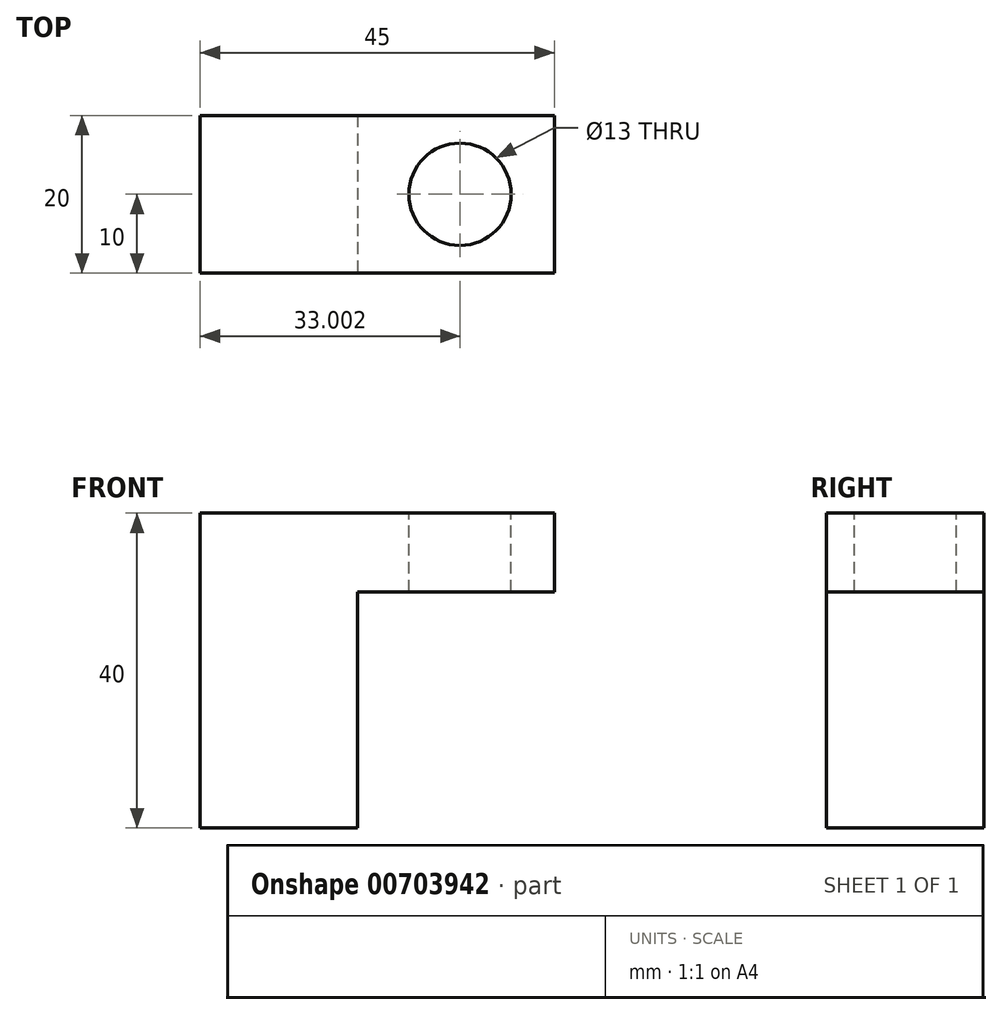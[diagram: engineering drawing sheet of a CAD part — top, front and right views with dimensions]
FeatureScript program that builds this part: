
annotation { "Feature Type Name" : "Feature", "Feature Type Description" : "" }
export const myFeature = defineFeature(function(context is Context, id is Id, definition is map)
    precondition{}
    {
        {
            var Q0;
            Q0=qCreatedBy(makeId("Top.planeOp"),FACE);
            var sketch = newSketch(context, id + "F0", { "sketchPlane" : qUnion([Q0])});
            skLineSegment(sketch, "E0", {"start": v(-97.99, 0) * mm, "end": v(96.27, 0) * mm, "construction": true});
            skLineSegment(sketch, "E1.bottom", {"start": v(-87.99, 10) * mm, "end": v(-107.99, 10) * mm});
            skLineSegment(sketch, "E1.top", {"start": v(-87.99, -10) * mm, "end": v(-107.99, -10) * mm});
            skLineSegment(sketch, "E1.left", {"start": v(-87.99, 10) * mm, "end": v(-87.99, -10) * mm});
            skLineSegment(sketch, "E1.right", {"start": v(-107.99, 10) * mm, "end": v(-107.99, -10) * mm});
            skPoint(sketch, "E1.middle", {"position": v(-97.99, 0) * mm});
            skSolve(sketch);
        }
        {
            var Q0;
            Q0 = qSketchRegion(id + "F0", true);
            extrude(context, id + "F1", {"entities" : qUnion([Q0]), "depth" : 40 * mm, "offsetDistance" : 25 * mm});
        }
        {
            var Q0;
            Q0=makeQuery(id+"F1.opExtrude","SWEPT_FACE",FACE,{"disambiguationData":[OSD([sQuery(id+"F0.wireOp",EDGE,"E1.left")])]});
            var sketch = newSketch(context, id + "F2", { "sketchPlane" : qUnion([Q0])});
            skLineSegment(sketch, "E2", {"start": v(-10, 40) * mm, "end": v(10, 40) * mm});
            skLineSegment(sketch, "E3", {"start": v(10, 40) * mm, "end": v(10, 30) * mm});
            skLineSegment(sketch, "E4", {"start": v(10, 30) * mm, "end": v(-10, 30) * mm});
            skLineSegment(sketch, "E5", {"start": v(-10, 30) * mm, "end": v(-10, 40) * mm});
            skSolve(sketch);
        }
        {
            var Q0;
            Q0 = qSketchRegion(id + "F2", true);
            extrude(context, id + "F3", {"entities" : qUnion([Q0]), "operationType" : NewBodyOperationType.ADD, "depth" : 25 * mm, "offsetDistance" : 25 * mm});
        }
        {
            var Q0;
            Q0=makeQuery(id+"F3.boolean.opBoolean","MERGE",FACE,{"derivedFrom":[makeQuery(id+"F1.opExtrude","CAP_FACE",FACE,{"disambiguationData":[OSD([sQuery(id+"F0.wireOp",EDGE,"E1.bottom"),sQuery(id+"F0.wireOp",EDGE,"E1.top"),sQuery(id+"F0.wireOp",EDGE,"E1.left"),sQuery(id+"F0.wireOp",EDGE,"E1.right")])],"isStart":false}),makeQuery(id+"F3.opExtrude","SWEPT_FACE",FACE,{"disambiguationData":[OSD([sQuery(id+"F2.wireOp",EDGE,"E2")])]})]});
            var sketch = newSketch(context, id + "F4", { "sketchPlane" : qUnion([Q0])});
            skLineSegment(sketch, "E6", {"start": v(-62.99, 0) * mm, "end": v(-74.99, 0) * mm, "construction": true});
            skCircle(sketch, "E7", {"center": v(-74.99, 0) * mm, "radius": 6.5 * mm});
            skSolve(sketch);
        }
        {
            var Q0;
            Q0 = qSketchRegion(id + "F4", true);
            extrude(context, id + "F5", {"entities" : qUnion([Q0]), "operationType" : NewBodyOperationType.REMOVE, "endBound" : BoundingType.THROUGH_ALL, "oppositeDirection" : true, "depth" : 25 * mm, "offsetDistance" : 25 * mm});
        }
    });
